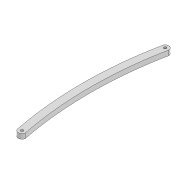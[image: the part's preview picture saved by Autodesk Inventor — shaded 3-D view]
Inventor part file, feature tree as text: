
AUTODESK INVENTOR PART (.ipt)
format: ipt  version: 2022 (Build 260153000, 153)  size: 94,208 bytes
history: native  units: mm
features: extrude x1, sketch x1
ambient origin geometry x8: Origin, YZ Plane, XZ Plane, XY Plane, X Axis, Y Axis, Z Axis, Center Point
bodies: Solid1 (feature_tree)
feature tree (2):
  extrude  "Extrusion1"  Depth=300.0mm
  sketch  "Sketch1"  dims[d0=2.2mm d1=2.2mm d2=6.0mm d3=116.798mm d6=4.0mm d7=0.0mm d14=300.0mm d15=300.0mm]
